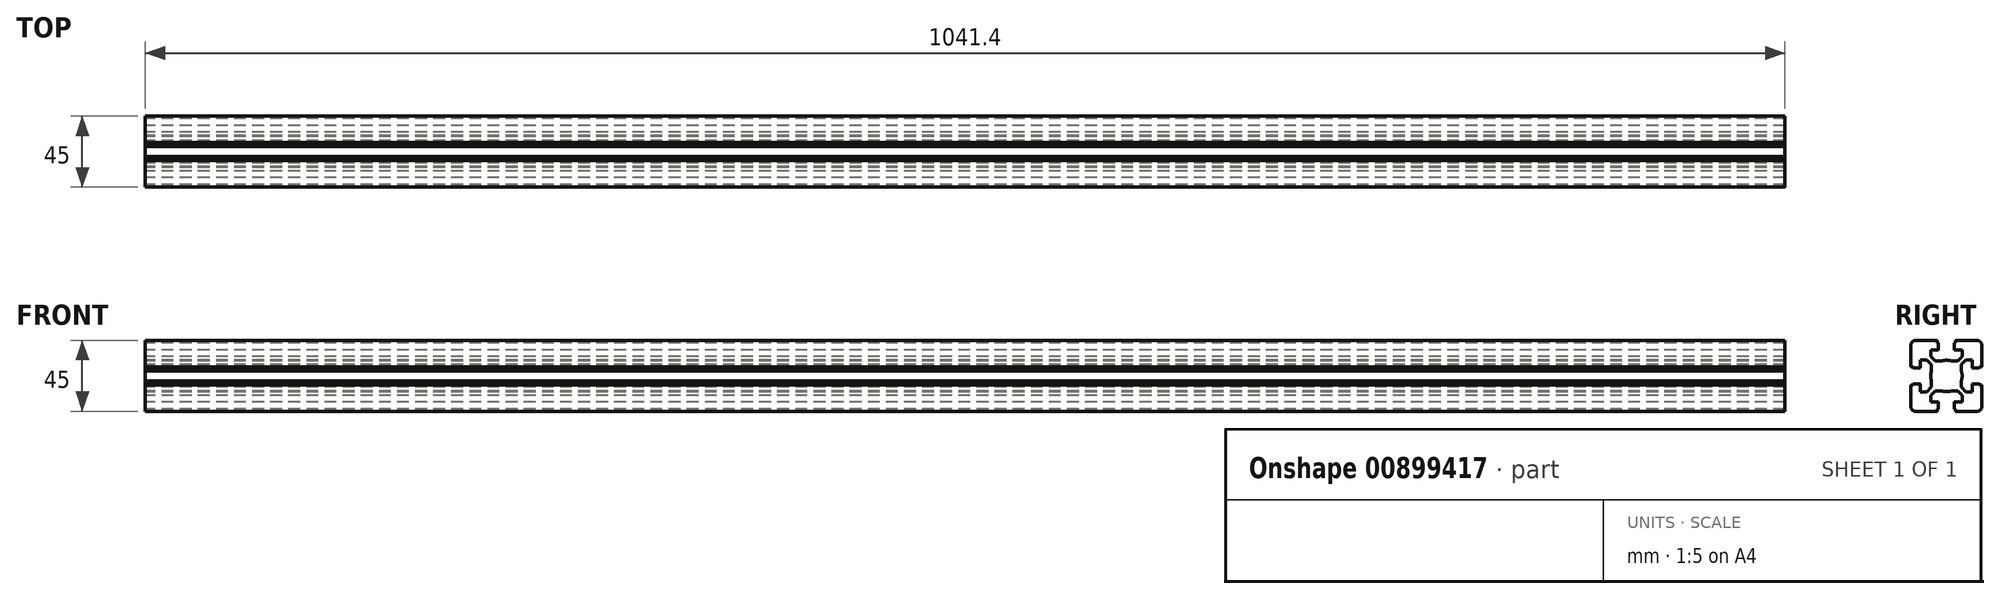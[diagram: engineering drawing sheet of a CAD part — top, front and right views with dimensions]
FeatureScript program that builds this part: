
annotation { "Feature Type Name" : "Feature", "Feature Type Description" : "" }
export const myFeature = defineFeature(function(context is Context, id is Id, definition is map)
    precondition{}
    {
        {
            var Q0;
            Q0=qCreatedBy(makeId("Right.planeOp"),FACE);
            var sketch = newSketch(context, id + "F0", { "sketchPlane" : qUnion([Q0])});
            skLineSegment(sketch, "E0", {"start": v(-20.09, -10.29) * mm, "end": v(-21.29, -10.29) * mm});
            skArc(sketch, "E1", {"start": v(-21.29, -10.29) * mm, "mid": v(-21.5, -10.38) * mm, "end": v(-21.59, -10.59) * mm});
            skLineSegment(sketch, "E2", {"start": v(-21.59, -10.59) * mm, "end": v(-21.59, -23.99) * mm});
            skArc(sketch, "E3", {"start": v(-21.59, -23.99) * mm, "mid": v(-20.7, -26.11) * mm, "end": v(-18.59, -26.99) * mm});
            skLineSegment(sketch, "E4", {"start": v(-18.59, -26.99) * mm, "end": v(-5.19, -26.99) * mm});
            skArc(sketch, "E5", {"start": v(-5.19, -26.99) * mm, "mid": v(-4.98, -26.9) * mm, "end": v(-4.89, -26.69) * mm});
            skLineSegment(sketch, "E6", {"start": v(-4.89, -26.69) * mm, "end": v(-4.89, -25.49) * mm});
            skLineSegment(sketch, "E7", {"start": v(-4.89, -25.49) * mm, "end": v(-4.39, -25.49) * mm});
            skArc(sketch, "E8", {"start": v(-4.39, -25.49) * mm, "mid": v(-4.18, -25.4) * mm, "end": v(-4.09, -25.19) * mm});
            skLineSegment(sketch, "E9", {"start": v(-4.09, -25.19) * mm, "end": v(-4.09, -21.29) * mm});
            skArc(sketch, "E10", {"start": v(-4.09, -21.29) * mm, "mid": v(-4.18, -21.08) * mm, "end": v(-4.39, -20.99) * mm});
            skLineSegment(sketch, "E11", {"start": v(-4.39, -20.99) * mm, "end": v(-9.14, -20.99) * mm});
            skLineSegment(sketch, "E12", {"start": v(-9.14, -20.99) * mm, "end": v(-9.14, -16.88) * mm});
            skLineSegment(sketch, "E13", {"start": v(-9.14, -16.88) * mm, "end": v(-6.25, -13.99) * mm});
            skLineSegment(sketch, "E14", {"start": v(-6.25, -13.99) * mm, "end": v(-2.21, -13.99) * mm});
            skArc(sketch, "E15", {"start": v(-2.21, -13.99) * mm, "mid": v(0.91, -14.49) * mm, "end": v(4.03, -13.99) * mm});
            skLineSegment(sketch, "E16", {"start": v(-20.09, -10.29) * mm, "end": v(-20.09, -9.79) * mm});
            skArc(sketch, "E17", {"start": v(-20.09, -9.79) * mm, "mid": v(-20, -9.58) * mm, "end": v(-19.79, -9.49) * mm});
            skLineSegment(sketch, "E18", {"start": v(-19.79, -9.49) * mm, "end": v(-15.89, -9.49) * mm});
            skArc(sketch, "E19", {"start": v(-15.89, -9.49) * mm, "mid": v(-15.68, -9.58) * mm, "end": v(-15.59, -9.79) * mm});
            skLineSegment(sketch, "E20", {"start": v(-15.59, -9.79) * mm, "end": v(-15.59, -14.54) * mm});
            skLineSegment(sketch, "E21", {"start": v(-15.59, -14.54) * mm, "end": v(-11.48, -14.54) * mm});
            skLineSegment(sketch, "E22", {"start": v(-11.48, -14.54) * mm, "end": v(-8.59, -11.65) * mm});
            skLineSegment(sketch, "E23", {"start": v(-8.59, -11.65) * mm, "end": v(-8.59, -7.61) * mm});
            skLineSegment(sketch, "E24", {"start": v(29.82, -4.49) * mm, "end": v(-31.05, -4.49) * mm});
            skLineSegment(sketch, "E25.MirrorCS", {"start": v(6.71, -25.49) * mm, "end": v(6.21, -25.49) * mm});
            skArc(sketch, "E26.MirrorCS", {"start": v(7.01, -26.99) * mm, "mid": v(6.8, -26.9) * mm, "end": v(6.71, -26.69) * mm});
            skLineSegment(sketch, "E27.MirrorCS", {"start": v(10.41, -11.65) * mm, "end": v(10.41, -7.61) * mm});
            skArc(sketch, "E28.MirrorCS", {"start": v(6.21, -25.49) * mm, "mid": v(6, -25.4) * mm, "end": v(5.91, -25.19) * mm});
            skLineSegment(sketch, "E29.MirrorCS", {"start": v(6.71, -26.69) * mm, "end": v(6.71, -25.49) * mm});
            skArc(sketch, "E30.MirrorCS", {"start": v(5.91, -21.29) * mm, "mid": v(6, -21.08) * mm, "end": v(6.21, -20.99) * mm});
            skLineSegment(sketch, "E31.MirrorCS", {"start": v(10.96, -16.88) * mm, "end": v(8.07, -13.99) * mm});
            skLineSegment(sketch, "E32.MirrorCS", {"start": v(13.3, -14.54) * mm, "end": v(10.41, -11.65) * mm});
            skLineSegment(sketch, "E33.MirrorCS", {"start": v(17.41, -14.54) * mm, "end": v(13.3, -14.54) * mm});
            skLineSegment(sketch, "E34.MirrorCS", {"start": v(17.41, -9.79) * mm, "end": v(17.41, -14.54) * mm});
            skLineSegment(sketch, "E35.MirrorCS", {"start": v(6.21, -20.99) * mm, "end": v(10.96, -20.99) * mm});
            skLineSegment(sketch, "E36.MirrorCS", {"start": v(8.07, -13.99) * mm, "end": v(4.03, -13.99) * mm});
            skArc(sketch, "E37.MirrorCS", {"start": v(4.03, -13.99) * mm, "mid": v(0.91, -14.49) * mm, "end": v(-2.21, -13.99) * mm});
            skLineSegment(sketch, "E38.MirrorCS", {"start": v(10.96, -20.99) * mm, "end": v(10.96, -16.88) * mm});
            skLineSegment(sketch, "E39.MirrorCS", {"start": v(5.91, -25.19) * mm, "end": v(5.91, -21.29) * mm});
            skArc(sketch, "E40.MirrorCS", {"start": v(23.41, -23.99) * mm, "mid": v(22.53, -26.11) * mm, "end": v(20.41, -26.99) * mm});
            skLineSegment(sketch, "E41.MirrorCS", {"start": v(20.41, -26.99) * mm, "end": v(7.01, -26.99) * mm});
            skLineSegment(sketch, "E42.MirrorCS", {"start": v(23.41, -10.59) * mm, "end": v(23.41, -23.99) * mm});
            skArc(sketch, "E43.MirrorCS", {"start": v(17.71, -9.49) * mm, "mid": v(17.5, -9.58) * mm, "end": v(17.41, -9.79) * mm});
            skArc(sketch, "E44.MirrorCS", {"start": v(23.11, -10.29) * mm, "mid": v(23.32, -10.38) * mm, "end": v(23.41, -10.59) * mm});
            skLineSegment(sketch, "E45.MirrorCS", {"start": v(21.91, -10.29) * mm, "end": v(21.91, -9.79) * mm});
            skLineSegment(sketch, "E46.MirrorCS", {"start": v(21.91, -10.29) * mm, "end": v(23.11, -10.29) * mm});
            skArc(sketch, "E47.MirrorCS", {"start": v(21.91, -9.79) * mm, "mid": v(21.82, -9.58) * mm, "end": v(21.61, -9.49) * mm});
            skLineSegment(sketch, "E48.MirrorCS", {"start": v(21.61, -9.49) * mm, "end": v(17.71, -9.49) * mm});
            skLineSegment(sketch, "E49.MirrorCS", {"start": v(6.71, 16.51) * mm, "end": v(6.21, 16.51) * mm});
            skArc(sketch, "E50.MirrorCS", {"start": v(-4.39, 16.51) * mm, "mid": v(-4.18, 16.42) * mm, "end": v(-4.09, 16.21) * mm});
            skLineSegment(sketch, "E51.MirrorCS", {"start": v(-4.89, 16.51) * mm, "end": v(-4.39, 16.51) * mm});
            skArc(sketch, "E52.MirrorCS", {"start": v(5.91, 12.31) * mm, "mid": v(6, 12.1) * mm, "end": v(6.21, 12.01) * mm});
            skLineSegment(sketch, "E53.MirrorCS", {"start": v(6.71, 17.71) * mm, "end": v(6.71, 16.51) * mm});
            skLineSegment(sketch, "E54.MirrorCS", {"start": v(-4.89, 17.71) * mm, "end": v(-4.89, 16.51) * mm});
            skArc(sketch, "E55.MirrorCS", {"start": v(-5.19, 18.01) * mm, "mid": v(-4.98, 17.92) * mm, "end": v(-4.89, 17.71) * mm});
            skArc(sketch, "E56.MirrorCS", {"start": v(-4.09, 12.31) * mm, "mid": v(-4.18, 12.1) * mm, "end": v(-4.39, 12.01) * mm});
            skArc(sketch, "E57.MirrorCS", {"start": v(7.01, 18.01) * mm, "mid": v(6.8, 17.92) * mm, "end": v(6.71, 17.71) * mm});
            skArc(sketch, "E58.MirrorCS", {"start": v(6.21, 16.51) * mm, "mid": v(6, 16.42) * mm, "end": v(5.91, 16.21) * mm});
            skArc(sketch, "E59.MirrorCS", {"start": v(23.11, 1.31) * mm, "mid": v(23.32, 1.4) * mm, "end": v(23.41, 1.61) * mm});
            skLineSegment(sketch, "E60.MirrorCS", {"start": v(21.91, 1.31) * mm, "end": v(21.91, 0.81) * mm});
            skArc(sketch, "E61.MirrorCS", {"start": v(-15.89, 0.51) * mm, "mid": v(-15.68, 0.6) * mm, "end": v(-15.59, 0.81) * mm});
            skArc(sketch, "E62.MirrorCS", {"start": v(-21.29, 1.31) * mm, "mid": v(-21.5, 1.4) * mm, "end": v(-21.59, 1.61) * mm});
            skArc(sketch, "E63.MirrorCS", {"start": v(17.71, 0.51) * mm, "mid": v(17.5, 0.6) * mm, "end": v(17.41, 0.81) * mm});
            skArc(sketch, "E64.MirrorCS", {"start": v(21.91, 0.81) * mm, "mid": v(21.82, 0.6) * mm, "end": v(21.61, 0.51) * mm});
            skLineSegment(sketch, "E65.MirrorCS", {"start": v(21.91, 1.31) * mm, "end": v(23.11, 1.31) * mm});
            skArc(sketch, "E66.MirrorCS", {"start": v(14.31, 5.31) * mm, "mid": v(14.1, 5.4) * mm, "end": v(14.01, 5.61) * mm});
            skArc(sketch, "E67.MirrorCS", {"start": v(-20.09, 0.81) * mm, "mid": v(-20, 0.6) * mm, "end": v(-19.79, 0.51) * mm});
            skLineSegment(sketch, "E68.MirrorCS", {"start": v(-20.09, 1.31) * mm, "end": v(-21.29, 1.31) * mm});
            skLineSegment(sketch, "E69.MirrorCS", {"start": v(-20.09, 1.31) * mm, "end": v(-20.09, 0.81) * mm});
            skLineSegment(sketch, "E70.MirrorCS", {"start": v(8.07, 5.01) * mm, "end": v(4.03, 5.01) * mm});
            skLineSegment(sketch, "E71.MirrorCS", {"start": v(-4.09, 16.21) * mm, "end": v(-4.09, 12.31) * mm});
            skLineSegment(sketch, "E72.MirrorCS", {"start": v(-9.14, 12.01) * mm, "end": v(-9.14, 7.9) * mm});
            skLineSegment(sketch, "E73.MirrorCS", {"start": v(-15.59, 5.56) * mm, "end": v(-11.48, 5.56) * mm});
            skLineSegment(sketch, "E74.MirrorCS", {"start": v(-4.39, 12.01) * mm, "end": v(-9.14, 12.01) * mm});
            skLineSegment(sketch, "E75.MirrorCS", {"start": v(-9.14, 7.9) * mm, "end": v(-6.25, 5.01) * mm});
            skLineSegment(sketch, "E76.MirrorCS", {"start": v(10.96, 12.01) * mm, "end": v(10.96, 7.9) * mm});
            skArc(sketch, "E77.MirrorCS", {"start": v(-21.59, 15.01) * mm, "mid": v(-20.7, 17.13) * mm, "end": v(-18.59, 18.01) * mm});
            skLineSegment(sketch, "E78.MirrorCS", {"start": v(23.41, 1.61) * mm, "end": v(23.41, 15.01) * mm});
            skLineSegment(sketch, "E79.MirrorCS", {"start": v(13.3, 5.56) * mm, "end": v(10.41, 2.67) * mm});
            skLineSegment(sketch, "E80.MirrorCS", {"start": v(-8.59, 2.67) * mm, "end": v(-8.59, -1.37) * mm});
            skLineSegment(sketch, "E81.MirrorCS", {"start": v(-15.59, 0.81) * mm, "end": v(-15.59, 5.56) * mm});
            skLineSegment(sketch, "E82.MirrorCS", {"start": v(10.41, 2.67) * mm, "end": v(10.41, -1.37) * mm});
            skLineSegment(sketch, "E83.MirrorCS", {"start": v(-18.59, 18.01) * mm, "end": v(-5.19, 18.01) * mm});
            skLineSegment(sketch, "E84.MirrorCS", {"start": v(10.96, 7.9) * mm, "end": v(8.07, 5.01) * mm});
            skLineSegment(sketch, "E85.MirrorCS", {"start": v(17.41, 5.56) * mm, "end": v(13.3, 5.56) * mm});
            skArc(sketch, "E86.MirrorCS", {"start": v(23.41, 15.01) * mm, "mid": v(22.53, 17.13) * mm, "end": v(20.41, 18.01) * mm});
            skLineSegment(sketch, "E87.MirrorCS", {"start": v(5.91, 16.21) * mm, "end": v(5.91, 12.31) * mm});
            skLineSegment(sketch, "E88.MirrorCS", {"start": v(17.41, 0.81) * mm, "end": v(17.41, 5.56) * mm});
            skLineSegment(sketch, "E89.MirrorCS", {"start": v(-11.48, 5.56) * mm, "end": v(-8.59, 2.67) * mm});
            skLineSegment(sketch, "E90.MirrorCS", {"start": v(-6.25, 5.01) * mm, "end": v(-2.21, 5.01) * mm});
            skLineSegment(sketch, "E91.MirrorCS", {"start": v(-21.59, 1.61) * mm, "end": v(-21.59, 15.01) * mm});
            skArc(sketch, "E92.MirrorCS", {"start": v(4.03, 5.01) * mm, "mid": v(0.91, 5.51) * mm, "end": v(-2.21, 5.01) * mm});
            skLineSegment(sketch, "E93.MirrorCS", {"start": v(6.21, 12.01) * mm, "end": v(10.96, 12.01) * mm});
            skArc(sketch, "E94.MirrorCS", {"start": v(-2.21, 5.01) * mm, "mid": v(0.91, 5.51) * mm, "end": v(4.03, 5.01) * mm});
            skLineSegment(sketch, "E95.MirrorCS", {"start": v(20.41, 18.01) * mm, "end": v(7.01, 18.01) * mm});
            skLineSegment(sketch, "E96.MirrorCS", {"start": v(-19.79, 0.51) * mm, "end": v(-15.89, 0.51) * mm});
            skLineSegment(sketch, "E97.MirrorCS", {"start": v(21.61, 0.51) * mm, "end": v(17.71, 0.51) * mm});
            skLineSegment(sketch, "E98.MirrorCS", {"start": v(0.91, -27.65) * mm, "end": v(0.91, 19.82) * mm});
            skArc(sketch, "E99", {"start": v(-8.59, -1.37) * mm, "mid": v(-9.09, -4.49) * mm, "end": v(-8.59, -7.61) * mm});
            skArc(sketch, "E100", {"start": v(10.41, -7.61) * mm, "mid": v(10.91, -4.49) * mm, "end": v(10.41, -1.37) * mm});
            skSolve(sketch);
        }
        {
            var Q0;
            Q0=qSketchRegion(id+"F0",true);
            extrude(context, id + "F1", {"entities" : qUnion([Q0]), "depth" : 1041.4 * mm, "offsetDistance" : 25.4 * mm});
        }
    });
